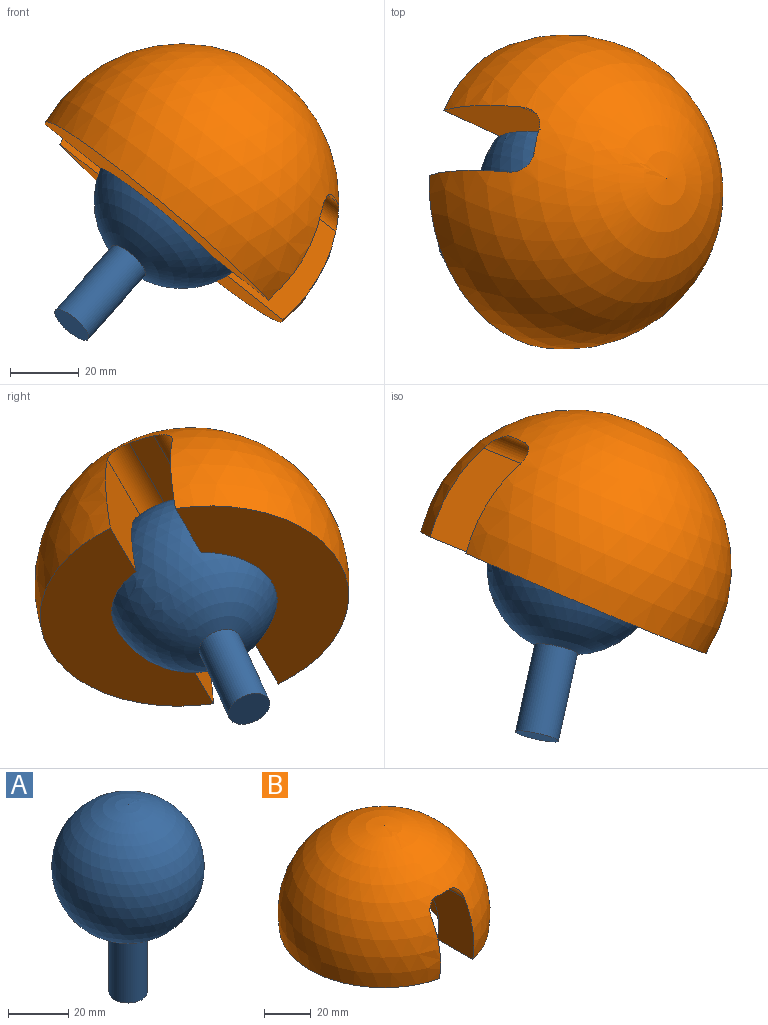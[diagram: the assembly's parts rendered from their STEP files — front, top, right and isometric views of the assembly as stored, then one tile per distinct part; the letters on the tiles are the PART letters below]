
ASSEMBLY  parts=2 mates=1
PART A: 3 faces, bbox 50.8x50.8x76.2 mm
  f0: sphere r=25.4mm, area 7978.6mm2, adj f1
  f1: cylinder r=6.35mm len=26.21mm, axis (0,0,-1), area 1045.6mm2, adj f0,f2
  f2: plane 12.7x12.7mm, normal (0,0,-1), area 126.7mm2, adj f1
PART B: 12 faces, bbox 91.4x91.4x53.6 mm
  f0: plane 87.67x34.9mm, normal (0,0,-1), area 1836.6mm2, adj f1,f2,f6,f7
  f1: sphere r=45.68mm, area 13881.9mm2, adj f0,f3,f5,f6,f7,f8,f9,f10
  f2: sphere r=25.4mm, area 1692.7mm2, adj f0,f6,f7,f11
  f3: plane 87.67x34.9mm, normal (0,0,-1), area 1836.6mm2, adj f1,f4,f8,f9
  f4: sphere r=25.4mm, area 1692.7mm2, adj f3,f8,f9,f10
  f5: plane 71.98x7.45mm, normal (0,0,-1), area 535.5mm2, adj f1,f10,f11
  f6: plane 36.21x29.74mm, normal (1,0,0), area 682.6mm2, adj f0,f1,f2,f11
  f7: plane 36.21x29.74mm, normal (1,0,0), area 682.6mm2, adj f0,f1,f2,f11
  f8: plane 36.21x29.74mm, normal (-1,0,0), area 682.6mm2, adj f1,f3,f4,f10
  f9: plane 36.21x29.74mm, normal (-1,0,0), area 682.6mm2, adj f1,f3,f4,f10
  f10: cylinder r=6.35mm len=77.74mm, axis (0,-1,0), area 715mm2, adj f1,f4,f5,f8,f9
  f11: cylinder r=6.35mm len=77.74mm, axis (0,-1,0), area 715mm2, adj f1,f2,f5,f6,f7
PLACE A rot(axis=(0.27,0.31,0.91),140.2deg) t=(-8.79,-2.76,17.94)mm
PLACE B rot(axis=(-0.36,0.19,-0.91),113.2deg) t=(-8.79,-2.76,17.94)mm
MATE ball A.f1 <-> B.f2  axis (0.63,0.33,0.71) through (-8.79,-2.76,17.94)mm
